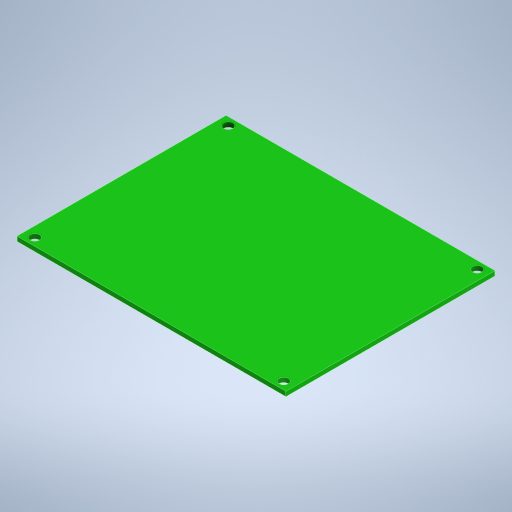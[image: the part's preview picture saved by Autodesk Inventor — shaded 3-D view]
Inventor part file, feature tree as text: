
AUTODESK INVENTOR PART (.ipt)
format: ipt  version: 2024 (Build 280153000, 153)  size: 227,328 bytes
history: native  units: in
note: dims shown in document units (in); Inventor stores cm internally (conversion verified against a paired STEP export)
features: extrude x2, sketch x2
ambient origin geometry x8: Origin, YZ Plane, XZ Plane, XY Plane, X Axis, Y Axis, Z Axis, Center Point
bodies: Solid1 (feature_tree)
feature tree (4):
  extrude  "Extrusion1"  Depth=0.06in
  extrude  "Extrusion2"  Depth=0.07in
  sketch  "Sketch1"  dims[d2=0.06in d3=0.0in d4=0.125in]
  sketch  "Sketch2"  dims[d5=0.04in d6=0.07in d7=0.04in d8=0.07in d9=0.04in d10=0.07in d11=0.04in d12=0.07in d13=1.0in d14=0.0in]
